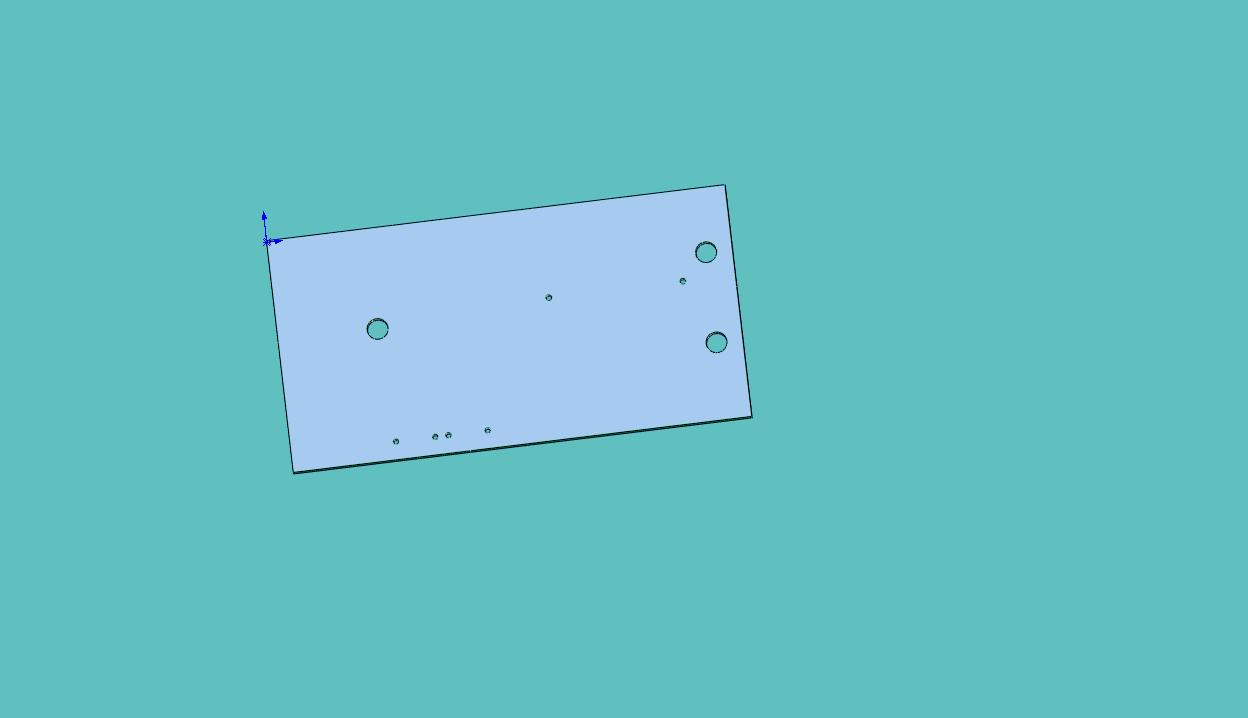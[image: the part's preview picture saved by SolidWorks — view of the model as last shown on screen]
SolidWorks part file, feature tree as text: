
SOLIDWORKS PART (.sldprt)
format: sldprt  version: not decoded by parser v0  size: 145,408 bytes
history: native  units: mm
features: sketch x4, cut_extrude x3, material x1, extrude x1 (+13 scaffold rows collapsed)
feature tree (22):
  scaffold x13  (default folders/planes/origin — collapsed)
  material  "Material <not specified>"
  sketch  "Sketch1"  dims[D1=88.9mm D2=45.72mm]
  extrude  "board shape -extrude"  Depth=1.5748mm
  sketch  "Sketch2"  dims[D1=1.1mm D2=1.1mm D3=26.0mm D4=10.16mm D5=27.94mm]
  cut_extrude  "mmc mount hole - cut"  Depth=1.5748mm
  sketch  "Sketch4"  dims[D1=1.016mm D2=1.016mm D3=1.016mm D4=1.016mm D5=3.556mm D6=7.62mm D7=2.54mm D8=7.62mm D9=50.8mm]
  cut_extrude  "HFBR anchor holes"  Depth=1.5748mm
  sketch  "Sketch5"  dims[c1.D1=~1.473759mm c1.D3=4.064mm c1.D4=4.064mm c1.D5=4.064mm c2.D1=15.24mm c2.D2=5.08mm c2.D6=17.78mm c2.D7=64.516mm c2.D8=10.668mm]
  cut_extrude  "Cut-Extrude3"  Depth=1.5748mm
decode coverage: 8 of 8 modeling features carry decoded parameters
note: ~ marks probable driven/reference dimensions
note: suppression state not decoded; provenance and decode notes live in map.json
